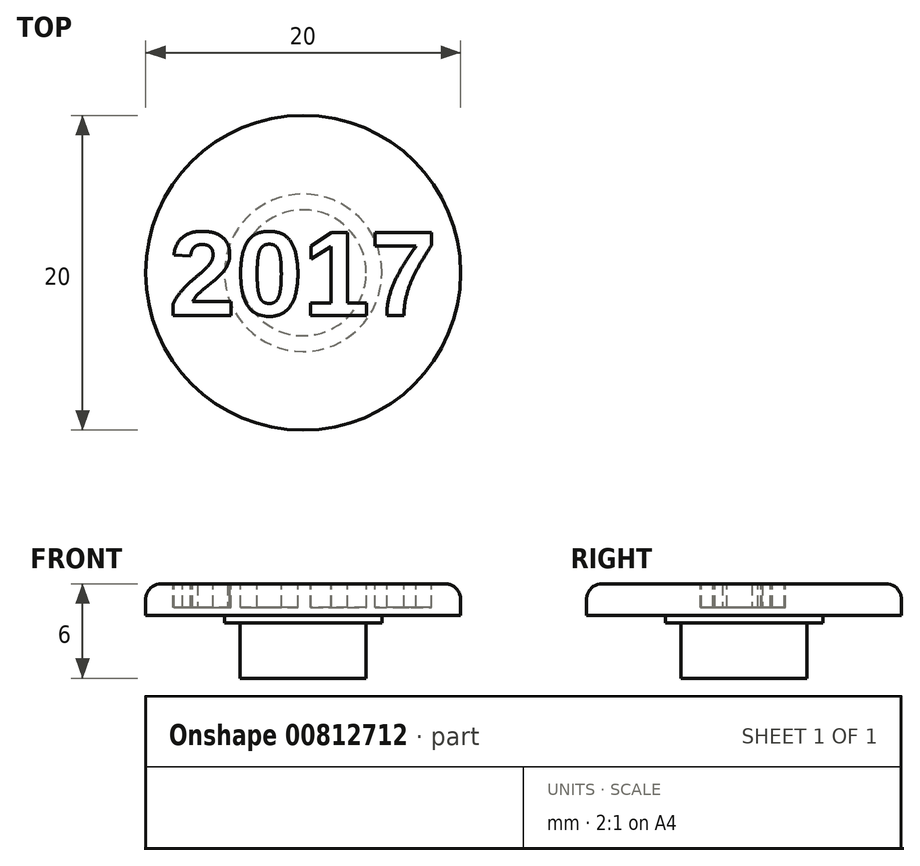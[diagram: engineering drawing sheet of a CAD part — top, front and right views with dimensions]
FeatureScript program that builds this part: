
annotation { "Feature Type Name" : "Feature", "Feature Type Description" : "" }
export const myFeature = defineFeature(function(context is Context, id is Id, definition is map)
    precondition{}
    {
        {
            var Q0;
            Q0=qCreatedBy(makeId("Top.planeOp"),FACE);
            var sketch = newSketch(context, id + "F0", { "sketchPlane" : qUnion([Q0])});
            skCircle(sketch, "E0", {"center": v(0, 0) * mm, "radius": 10 * mm});
            skCircle(sketch, "E1", {"center": v(0, 0) * mm, "radius": 4 * mm});
            skCircle(sketch, "E2", {"center": v(0, 0) * mm, "radius": 5 * mm});
            skSolve(sketch);
        }
        {
            var Q0;
            Q0=makeQuery(id+"F0.imprint","IMPRINT",FACE,{"disambiguationData":[TD([[makeQuery(id+"F0.imprint","IMPRINT",EDGE,{"derivedFrom":sQuery(id+"F0.wireOp",EDGE,"E1")}),1.0]])]});
            extrude(context, id + "F1", {"entities" : qUnion([Q0]), "oppositeDirection" : true, "depth" : 6 * mm, "offsetDistance" : 25 * mm});
        }
        {
            var Q0;
            Q0=makeQuery(id+"F0.imprint","IMPRINT",FACE,{"disambiguationData":[TD([[makeQuery(id+"F0.imprint","IMPRINT",EDGE,{"derivedFrom":sQuery(id+"F0.wireOp",EDGE,"E1")}),-1.0]])]});
            extrude(context, id + "F2", {"entities" : qUnion([Q0]), "operationType" : NewBodyOperationType.ADD, "oppositeDirection" : true, "depth" : 2.5 * mm, "offsetDistance" : 25 * mm});
        }
        {
            var Q0;
            Q0=makeQuery(id+"F0.imprint","IMPRINT",FACE,{"disambiguationData":[TD([[makeQuery(id+"F0.imprint","IMPRINT",EDGE,{"derivedFrom":sQuery(id+"F0.wireOp",EDGE,"E0")}),1.0]])]});
            extrude(context, id + "F3", {"entities" : qUnion([Q0]), "operationType" : NewBodyOperationType.ADD, "oppositeDirection" : true, "depth" : 2 * mm, "offsetDistance" : 25 * mm});
        }
        {
            var Q0;
            Q0=makeQuery(id+"F3.opExtrude","CAP_EDGE",EDGE,{"disambiguationData":[OSD([sQuery(id+"F0.wireOp",EDGE,"E0")])],"isStart":true});
            fillet(context, id + "F4", {"entities" : qUnion([Q0]), "radius" : 1 * mm, "tangentPropagation" : true, "allowEdgeOverflow" : false});
        }
        {
            var Q0;
            Q0=qCreatedBy(makeId("Top.planeOp"),FACE);
            var sketch = newSketch(context, id + "F5", { "sketchPlane" : qUnion([Q0])});
            skText(sketch, "E3", { "text": "2017", "fontName": "Arimo-Bold.ttf"});
            const initialGuessF5  = {"E3": [-0.00852, -0.0027, 1, 0, 0.0055]};
            skSetInitialGuess(sketch, initialGuessF5);
            skSolve(sketch);
        }
        {
            var Q0;
            Q0=qSketchRegion(id+"F5",true);
            extrude(context, id + "F6", {"entities" : qUnion([Q0]), "operationType" : NewBodyOperationType.REMOVE, "oppositeDirection" : true, "depth" : 1.5 * mm, "offsetDistance" : 25 * mm});
        }
    });
